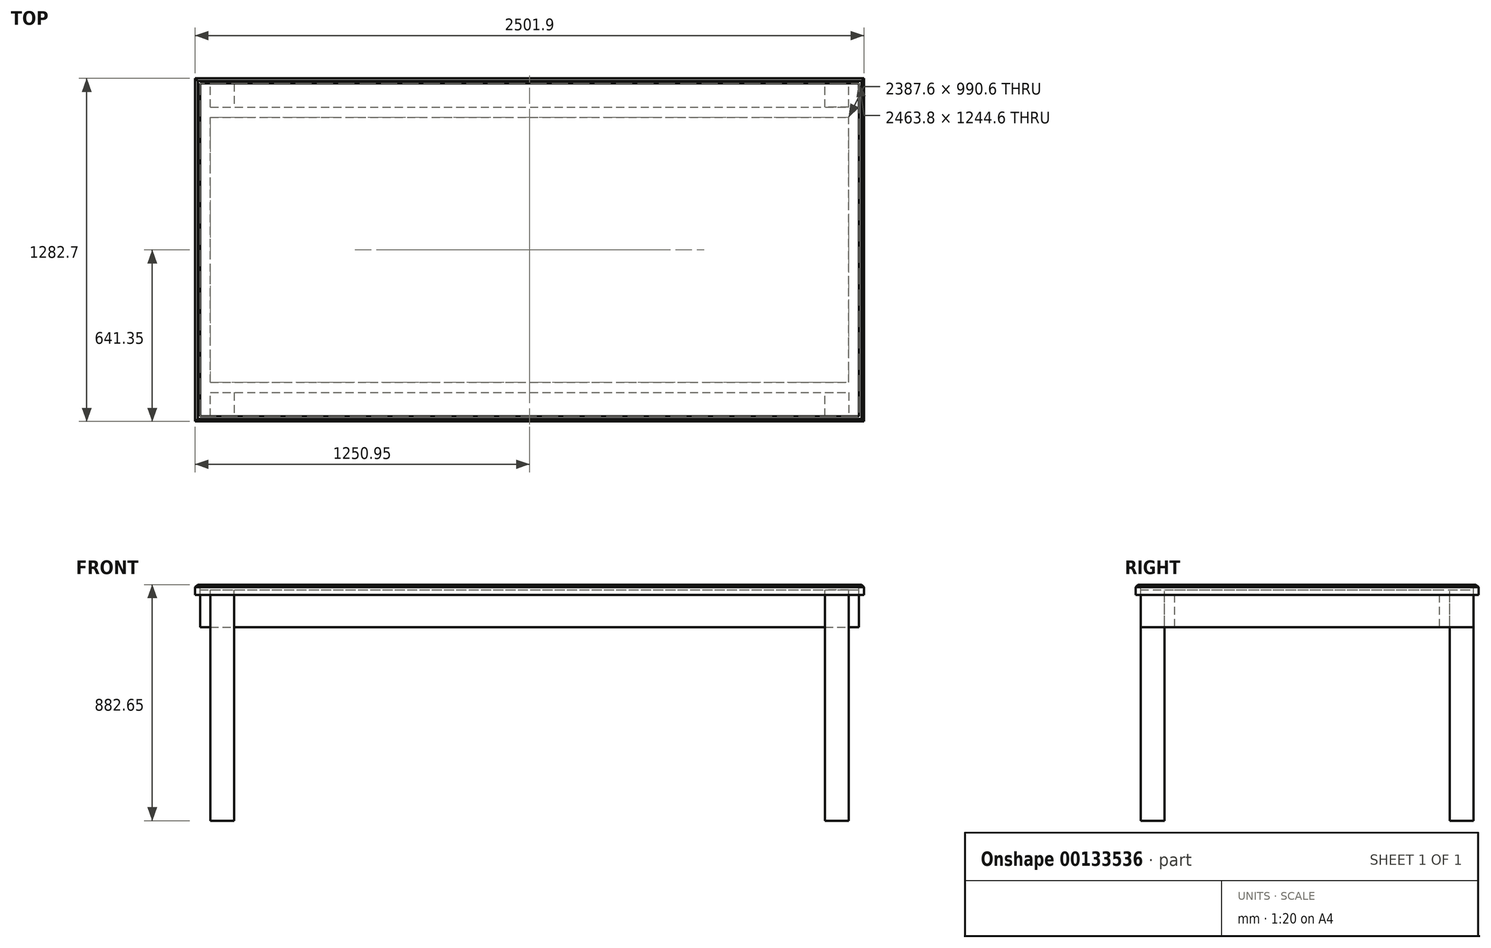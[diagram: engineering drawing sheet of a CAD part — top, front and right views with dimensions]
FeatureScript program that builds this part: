
annotation { "Feature Type Name" : "Feature", "Feature Type Description" : "" }
export const myFeature = defineFeature(function(context is Context, id is Id, definition is map)
    precondition{}
    {
        {
            var Q0;
            Q0=qCreatedBy(makeId("Top.planeOp"),FACE);
            var sketch = newSketch(context, id + "F0", { "sketchPlane" : qUnion([Q0])});
            skLineSegment(sketch, "E0.bottom", {"start": v(-1231.9, -622.3) * mm, "end": v(1231.9, -622.3) * mm});
            skLineSegment(sketch, "E0.top", {"start": v(-1231.9, 622.3) * mm, "end": v(1231.9, 622.3) * mm});
            skLineSegment(sketch, "E0.left", {"start": v(-1231.9, -622.3) * mm, "end": v(-1231.9, 622.3) * mm});
            skLineSegment(sketch, "E0.right", {"start": v(1231.9, -622.3) * mm, "end": v(1231.9, 622.3) * mm});
            skPoint(sketch, "E0.middle", {"position": v(0, 0) * mm});
            skLineSegment(sketch, "E1.0", {"start": v(-1250.95, 641.35) * mm, "end": v(1250.95, 641.35) * mm});
            skLineSegment(sketch, "E1.1", {"start": v(-1250.95, -641.35) * mm, "end": v(-1250.95, 641.35) * mm});
            skLineSegment(sketch, "E1.2", {"start": v(-1250.95, -641.35) * mm, "end": v(1250.95, -641.35) * mm});
            skLineSegment(sketch, "E1.3", {"start": v(1250.95, -641.35) * mm, "end": v(1250.95, 641.35) * mm});
            skSolve(sketch);
        }
        {
            var Q0;
            Q0=makeQuery(id+"F0.imprint","IMPRINT",FACE,{"disambiguationData":[TD([[makeQuery(id+"F0.imprint","IMPRINT",EDGE,{"derivedFrom":sQuery(id+"F0.wireOp",EDGE,"E0.bottom")}),1.0]])]});
            extrude(context, id + "F1", {"entities" : qUnion([Q0]), "oppositeDirection" : true, "depth" : 19.05 * mm});
        }
        {
            var Q0;
            Q0=makeQuery(id+"F0.imprint","IMPRINT",FACE,{"disambiguationData":[TD([[makeQuery(id+"F0.imprint","IMPRINT",EDGE,{"derivedFrom":sQuery(id+"F0.wireOp",EDGE,"E0.bottom")}),-1.0]])]});
            extrude(context, id + "F2", {"entities" : qUnion([Q0]), "oppositeDirection" : true, "depth" : 38.1 * mm});
        }
        {
            var Q0;
            Q0=makeQuery(id+"F2.opExtrude","CAP_EDGE",EDGE,{"disambiguationData":[OSD([sQuery(id+"F0.wireOp",EDGE,"E1.2")])],"isStart":true});
            var Q1;
            Q1=makeQuery(id+"F2.opExtrude","CAP_EDGE",EDGE,{"disambiguationData":[OSD([sQuery(id+"F0.wireOp",EDGE,"E1.1")])],"isStart":true});
            var Q2;
            Q2=makeQuery(id+"F2.opExtrude","CAP_EDGE",EDGE,{"disambiguationData":[OSD([sQuery(id+"F0.wireOp",EDGE,"E1.0")])],"isStart":true});
            var Q3;
            Q3=makeQuery(id+"F2.opExtrude","CAP_EDGE",EDGE,{"disambiguationData":[OSD([sQuery(id+"F0.wireOp",EDGE,"E1.3")])],"isStart":true});
            chamfer(context, id + "F3", {"entities" : qUnion([Q0, Q1, Q2, Q3]), "width" : 9.52 * mm, "tangentPropagation" : true});
        }
        {
            var Q0;
            Q0=makeQuery(id+"F1.opExtrude","CAP_FACE",FACE,{"disambiguationData":[OSD([sQuery(id+"F0.wireOp",EDGE,"E0.bottom"),sQuery(id+"F0.wireOp",EDGE,"E0.top"),sQuery(id+"F0.wireOp",EDGE,"E0.left"),sQuery(id+"F0.wireOp",EDGE,"E0.right")])],"isStart":false});
            var sketch = newSketch(context, id + "F4", { "sketchPlane" : qUnion([Q0])});
            skLineSegment(sketch, "E2.0", {"start": v(-1231.9, 622.3) * mm, "end": v(-1193.8, 622.3) * mm});
            skLineSegment(sketch, "E2.1", {"start": v(-1231.9, 622.3) * mm, "end": v(-1231.9, -622.3) * mm});
            skLineSegment(sketch, "E2.2", {"start": v(-1231.9, -622.3) * mm, "end": v(-1193.8, -622.3) * mm});
            skLineSegment(sketch, "E2.3", {"start": v(1231.9, 622.3) * mm, "end": v(1231.9, -622.3) * mm});
            skLineSegment(sketch, "E3.1", {"start": v(-1193.8, 495.3) * mm, "end": v(-1193.8, -495.3) * mm});
            skLineSegment(sketch, "E3.2", {"start": v(-1193.8, -495.3) * mm, "end": v(1193.8, -495.3) * mm});
            skLineSegment(sketch, "E3.3", {"start": v(1193.8, 495.3) * mm, "end": v(1193.8, -495.3) * mm});
            skLineSegment(sketch, "E4", {"start": v(-1193.8, 495.3) * mm, "end": v(1193.8, 495.3) * mm});
            skLineSegment(sketch, "E5", {"start": v(-1193.8, 622.3) * mm, "end": v(-1193.8, 533.4) * mm});
            skLineSegment(sketch, "E6", {"start": v(-1193.8, 533.4) * mm, "end": v(1193.8, 533.4) * mm});
            skLineSegment(sketch, "E7", {"start": v(1193.8, 533.4) * mm, "end": v(1193.8, 622.3) * mm});
            skLineSegment(sketch, "E8.trimOffspring", {"start": v(1193.8, 622.3) * mm, "end": v(1231.9, 622.3) * mm});
            skLineSegment(sketch, "E9", {"start": v(-1193.8, -533.4) * mm, "end": v(-1193.8, -622.3) * mm});
            skLineSegment(sketch, "E10", {"start": v(-1193.8, -533.4) * mm, "end": v(1193.8, -533.4) * mm});
            skLineSegment(sketch, "E11", {"start": v(1193.8, -533.4) * mm, "end": v(1193.8, -622.3) * mm});
            skLineSegment(sketch, "E12.trimOffspring", {"start": v(1193.8, -622.3) * mm, "end": v(1231.9, -622.3) * mm});
            skSolve(sketch);
        }
        {
            var Q0;
            Q0 = qSketchRegion(id + "F4", true);
            extrude(context, id + "F5", {"entities" : qUnion([Q0]), "depth" : 139.7 * mm});
        }
        {
            var Q0;
            Q0=makeQuery(id+"F1.opExtrude","CAP_FACE",FACE,{"disambiguationData":[OSD([sQuery(id+"F0.wireOp",EDGE,"E0.bottom"),sQuery(id+"F0.wireOp",EDGE,"E0.top"),sQuery(id+"F0.wireOp",EDGE,"E0.left"),sQuery(id+"F0.wireOp",EDGE,"E0.right")])],"isStart":false});
            var sketch = newSketch(context, id + "F6", { "sketchPlane" : qUnion([Q0])});
            skLineSegment(sketch, "E13.bottom", {"start": v(-1193.8, -533.4) * mm, "end": v(-1104.9, -533.4) * mm});
            skLineSegment(sketch, "E13.top", {"start": v(-1193.8, -622.3) * mm, "end": v(-1104.9, -622.3) * mm});
            skLineSegment(sketch, "E13.left", {"start": v(-1193.8, -622.3) * mm, "end": v(-1193.8, -533.4) * mm});
            skLineSegment(sketch, "E13.right", {"start": v(-1104.9, -622.3) * mm, "end": v(-1104.9, -533.4) * mm});
            skLineSegment(sketch, "E14.bottom", {"start": v(-1193.8, 533.4) * mm, "end": v(-1104.9, 533.4) * mm});
            skLineSegment(sketch, "E14.top", {"start": v(-1193.8, 622.3) * mm, "end": v(-1104.9, 622.3) * mm});
            skLineSegment(sketch, "E14.left", {"start": v(-1193.8, 533.4) * mm, "end": v(-1193.8, 622.3) * mm});
            skLineSegment(sketch, "E14.right", {"start": v(-1104.9, 533.4) * mm, "end": v(-1104.9, 622.3) * mm});
            skLineSegment(sketch, "E15.bottom", {"start": v(1193.8, -533.4) * mm, "end": v(1104.9, -533.4) * mm});
            skLineSegment(sketch, "E15.top", {"start": v(1193.8, -622.3) * mm, "end": v(1104.9, -622.3) * mm});
            skLineSegment(sketch, "E15.left", {"start": v(1193.8, -533.4) * mm, "end": v(1193.8, -622.3) * mm});
            skLineSegment(sketch, "E15.right", {"start": v(1104.9, -533.4) * mm, "end": v(1104.9, -622.3) * mm});
            skLineSegment(sketch, "E16.bottom", {"start": v(1104.9, 622.3) * mm, "end": v(1193.8, 622.3) * mm});
            skLineSegment(sketch, "E16.top", {"start": v(1104.9, 533.4) * mm, "end": v(1193.8, 533.4) * mm});
            skLineSegment(sketch, "E16.left", {"start": v(1104.9, 622.3) * mm, "end": v(1104.9, 533.4) * mm});
            skLineSegment(sketch, "E16.right", {"start": v(1193.8, 622.3) * mm, "end": v(1193.8, 533.4) * mm});
            skSolve(sketch);
        }
        {
            var Q0;
            Q0 = qSketchRegion(id + "F6", true);
            extrude(context, id + "F7", {"entities" : qUnion([Q0]), "depth" : 863.6 * mm});
        }
    });
